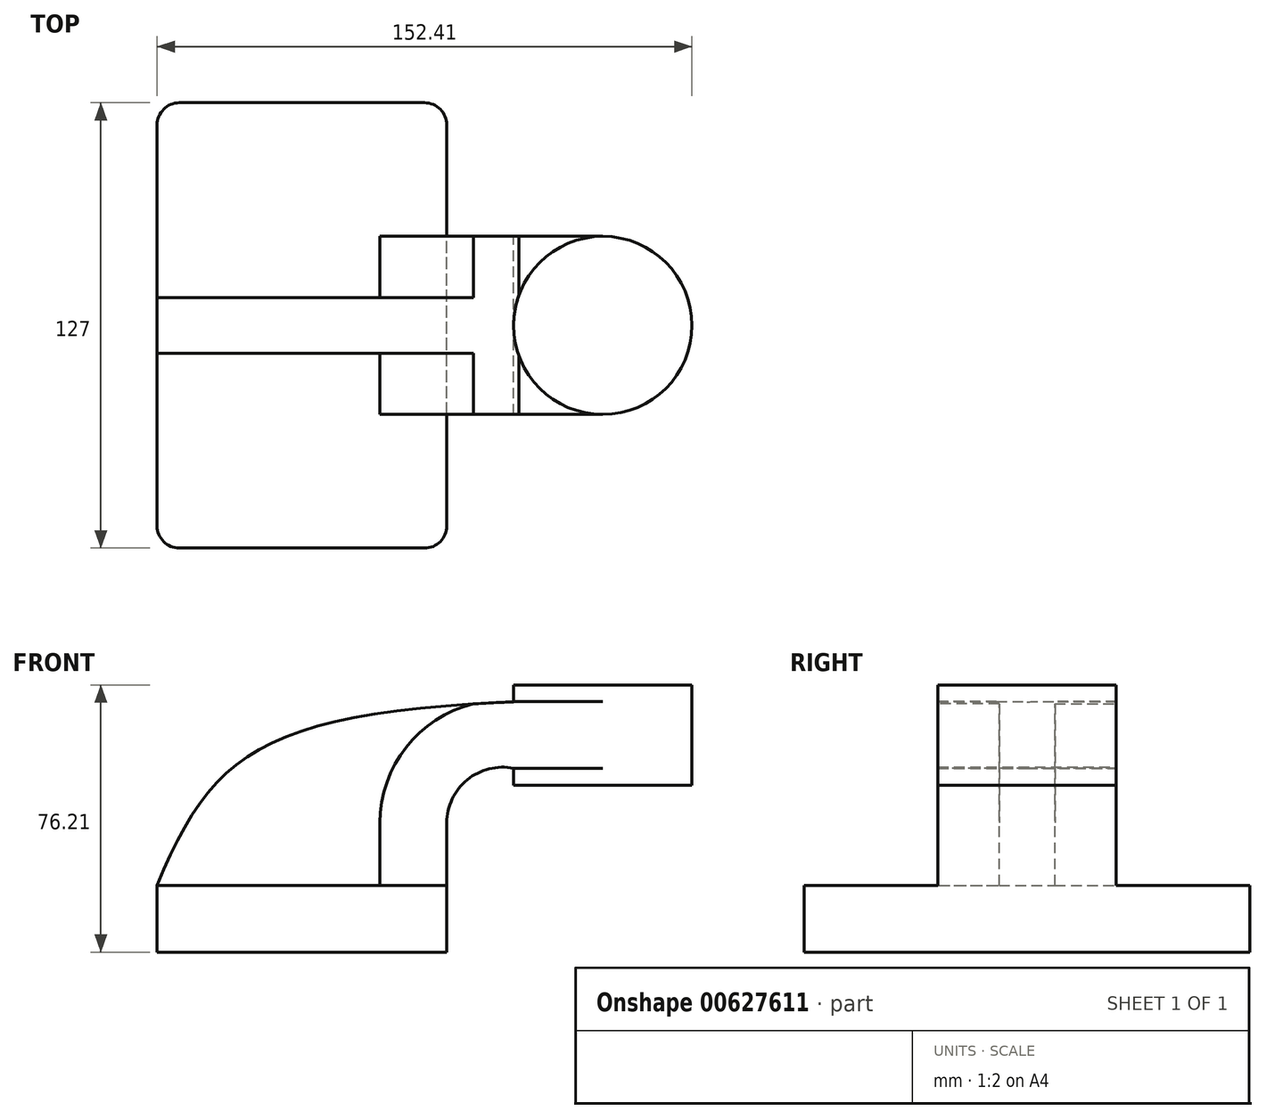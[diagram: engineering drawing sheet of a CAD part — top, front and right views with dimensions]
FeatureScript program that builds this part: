
annotation { "Feature Type Name" : "Feature", "Feature Type Description" : "" }
export const myFeature = defineFeature(function(context is Context, id is Id, definition is map)
    precondition{}
    {
        {
            var Q0;
            Q0=qCreatedBy(makeId("Front.planeOp"),FACE);
            var sketch = newSketch(context, id + "F0", { "sketchPlane" : qUnion([Q0])});
            skLineSegment(sketch, "E0.bottom", {"start": v(-41.27, 9.53) * mm, "end": v(41.28, 9.53) * mm});
            skLineSegment(sketch, "E0.top", {"start": v(-41.28, -9.52) * mm, "end": v(41.27, -9.52) * mm});
            skLineSegment(sketch, "E0.left", {"start": v(-41.28, 9.53) * mm, "end": v(-41.28, -9.52) * mm});
            skLineSegment(sketch, "E0.right", {"start": v(41.28, 9.53) * mm, "end": v(41.27, -9.52) * mm});
            skPoint(sketch, "E0.middle", {"position": v(0, 0) * mm});
            skLineSegment(sketch, "E1.bottom", {"start": v(60.33, 66.68) * mm, "end": v(111.12, 66.68) * mm});
            skLineSegment(sketch, "E1.top", {"start": v(60.33, 38.1) * mm, "end": v(111.12, 38.1) * mm});
            skLineSegment(sketch, "E1.left", {"start": v(60.33, 66.68) * mm, "end": v(60.33, 38.1) * mm});
            skLineSegment(sketch, "E1.right", {"start": v(111.12, 66.68) * mm, "end": v(111.12, 38.1) * mm});
            skPoint(sketch, "E1.middle", {"position": v(85.72, 52.39) * mm});
            skLineSegment(sketch, "E2", {"start": v(41.28, 9.53) * mm, "end": v(41.28, 27.32) * mm});
            skArc(sketch, "E3", {"start": v(41.27, 27.32) * mm, "mid": v(47.1, 39.62) * mm, "end": v(60.33, 42.88) * mm});
            skLineSegment(sketch, "E4", {"start": v(60.33, 42.88) * mm, "end": v(85.72, 42.88) * mm});
            skLineSegment(sketch, "E5.0", {"start": v(61.87, 61.93) * mm, "end": v(85.72, 61.93) * mm});
            skArc(sketch, "E5.1", {"start": v(22.23, 27.32) * mm, "mid": v(34.18, 53.63) * mm, "end": v(61.87, 61.93) * mm});
            skLineSegment(sketch, "E5.2", {"start": v(22.22, 9.53) * mm, "end": v(22.22, 27.32) * mm});
            skFitSpline(sketch, "E6", {"points": [v(-41.28, 9.52) * mm, v(61.87, 61.93) * mm], "startDerivative": vector(46.84, 113.63) * mm, "endDerivative": vector(218.9, 9.28) * mm});
            skLineSegment(sketch, "E7", {"start": v(85.72, 38.1) * mm, "end": v(85.72, 66.68) * mm});
            skSolve(sketch);
        }
        {
            var Q0;
            Q0=makeQuery(id+"F0.imprint","IMPRINT",FACE,{"disambiguationData":[TD([[makeQuery(id+"F0.imprint","IMPRINT",EDGE,{"derivedFrom":sQuery(id+"F0.wireOp",EDGE,"E0.top")}),1.0]])]});
            extrude(context, id + "F1", {"entities" : qUnion([Q0]), "endBound" : BoundingType.SYMMETRIC, "depth" : 127 * mm, "offsetDistance" : 25.4 * mm});
        }
        {
            var Q0;
            {var subQ6=sQuery(id+"F0.wireOp",EDGE,"E2");Q0=makeQuery(id+"F0.imprint","IMPRINT",FACE,{"disambiguationData":[TD([[makeQuery(id+"F0.imprint","IMPRINT",EDGE,{"derivedFrom":subQ6}),1.0]])]});}
            var Q1;
            {var subQ1=sQuery(id+"F0.wireOp",EDGE,"E4");Q1=makeQuery(id+"F0.imprint","IMPRINT",FACE,{"disambiguationData":[TD([[makeQuery(id+"F0.imprint","IMPRINT",EDGE,{"derivedFrom":subQ1}),1.0]])]});}
            extrude(context, id + "F2", {"entities" : qUnion([Q0, Q1]), "operationType" : NewBodyOperationType.ADD, "endBound" : BoundingType.SYMMETRIC, "depth" : 50.8 * mm, "offsetDistance" : 25.4 * mm});
        }
        {
            var Q0;
            {var subQ3=sQuery(id+"F0.wireOp",EDGE,"E5.2");Q0=makeQuery(id+"F0.imprint","IMPRINT",FACE,{"disambiguationData":[TD([[makeQuery(id+"F0.imprint","IMPRINT",EDGE,{"derivedFrom":subQ3}),1.0]])]});}
            extrude(context, id + "F3", {"entities" : qUnion([Q0]), "operationType" : NewBodyOperationType.ADD, "endBound" : BoundingType.SYMMETRIC, "depth" : 15.88 * mm, "offsetDistance" : 25.4 * mm});
        }
        {
            var Q0;
            {var subQ4=sQuery(id+"F0.wireOp",EDGE,"E1.right");Q0=makeQuery(id+"F0.imprint","IMPRINT",FACE,{"disambiguationData":[TD([[makeQuery(id+"F0.imprint","IMPRINT",EDGE,{"derivedFrom":subQ4}),-1.0]])]});}
            var Q1;
            Q1=sQuery(id+"F0.wireOp",EDGE,"E7");
            revolve(context, id + "F4", {"operationType" : NewBodyOperationType.ADD, "entities" : qUnion([Q0]), "axis" : qUnion([Q1]), "revolveType" : RevolveType.FULL});
        }
        {
            var Q0;
            Q0=makeQuery(id+"F1.opExtrude","CAP_EDGE",EDGE,{"disambiguationData":[OSD([sQuery(id+"F0.wireOp",EDGE,"E0.right")])],"isStart":false});
            fillet(context, id + "F5", {"entities" : qUnion([Q0]), "radius" : 6.35 * mm, "tangentPropagation" : true, "allowEdgeOverflow" : false});
        }
        {
            var Q0;
            Q0=makeQuery(id+"F1.opExtrude","CAP_EDGE",EDGE,{"disambiguationData":[OSD([sQuery(id+"F0.wireOp",EDGE,"E0.left")])],"isStart":false});
            fillet(context, id + "F6", {"entities" : qUnion([Q0]), "radius" : 6.35 * mm, "tangentPropagation" : true, "allowEdgeOverflow" : false});
        }
        {
            var Q0;
            Q0=makeQuery(id+"F1.opExtrude","CAP_EDGE",EDGE,{"disambiguationData":[OSD([sQuery(id+"F0.wireOp",EDGE,"E0.left")])],"isStart":true});
            fillet(context, id + "F7", {"entities" : qUnion([Q0]), "radius" : 6.35 * mm, "tangentPropagation" : true, "allowEdgeOverflow" : false});
        }
        {
            var Q0;
            Q0=makeQuery(id+"F1.opExtrude","CAP_EDGE",EDGE,{"disambiguationData":[OSD([sQuery(id+"F0.wireOp",EDGE,"E0.right")])],"isStart":true});
            fillet(context, id + "F8", {"entities" : qUnion([Q0]), "radius" : 6.35 * mm, "tangentPropagation" : true, "allowEdgeOverflow" : false});
        }
    });
